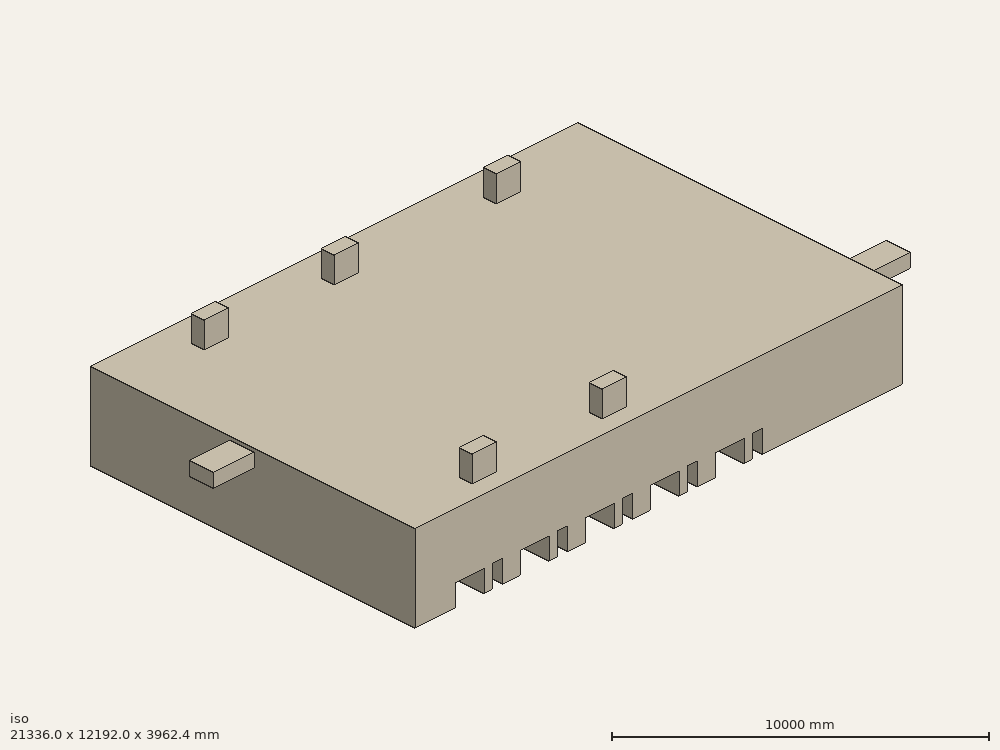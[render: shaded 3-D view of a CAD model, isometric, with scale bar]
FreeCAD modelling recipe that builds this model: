
FCSTD DOCUMENT  (FreeCAD 0.18R14555 (Git shallow))
Label: flow_domain
License: All rights reserved
LicenseURL: http://en.wikipedia.org/wiki/All_rights_reserved
objects: Part::Box×19, Part::MultiFuse×12, Part::Mirroring×1, Part::Cut×1
note: 33 computed .brp shape members not serialized (recipe doc carries the construction recipe); baked Part::Feature solids carry a one-line shape summary decoded from their .brp

FEATURE [Part::Box] Box001  label="Bed 1"
  AttacherType = Attacher::AttachEngine3D
  Height = 762
  Length = 1066.8
  Width = 1981.2
FEATURE [Part::Box] Box002  label="Table 1"
  AttacherType = Attacher::AttachEngine3D
  Height = 798.576
  Length = 396.24
  Placement = pos=(1371.6,0,0) rot=(0,0,1;0rad)
  Width = 396.24
FEATURE [Part::MultiFuse] Fusion  label="Set 1"
  Shapes = -> [Box002,Box001]
FEATURE [Part::Box] Box003  label="Bed 002"
  AttacherType = Attacher::AttachEngine3D
  Height = 762
  Length = 1066.8
  Width = 1981.2
FEATURE [Part::Box] Box004  label="Table 002"
  AttacherType = Attacher::AttachEngine3D
  Height = 798.576
  Length = 396.24
  Placement = pos=(1371.6,0,0) rot=(0,0,1;0rad)
  Width = 396.24
FEATURE [Part::MultiFuse] Fusion001  label="Set 2"
  Placement = pos=(2438.4,0,0) rot=(0,0,1;0rad)
  Shapes = -> [Box004,Box003]
FEATURE [Part::Box] Box005  label="Table 003"
  AttacherType = Attacher::AttachEngine3D
  Height = 798.576
  Length = 396.24
  Placement = pos=(1371.6,0,0) rot=(0,0,1;0rad)
  Width = 396.24
FEATURE [Part::Box] Box006  label="Bed 003"
  AttacherType = Attacher::AttachEngine3D
  Height = 762
  Length = 1066.8
  Width = 1981.2
FEATURE [Part::MultiFuse] Fusion002  label="Set 3"
  Placement = pos=(4876.8,0,0) rot=(0,0,1;0rad)
  Shapes = -> [Box005,Box006]
FEATURE [Part::Box] Box007  label="Bed 004"
  AttacherType = Attacher::AttachEngine3D
  Height = 762
  Length = 1066.8
  Width = 1981.2
FEATURE [Part::Box] Box008  label="Table 004"
  AttacherType = Attacher::AttachEngine3D
  Height = 798.576
  Length = 396.24
  Placement = pos=(1371.6,0,0) rot=(0,0,1;0rad)
  Width = 396.24
FEATURE [Part::MultiFuse] Fusion003  label="Set 4"
  Placement = pos=(7315.2,0,0) rot=(0,0,1;0rad)
  Shapes = -> [Box008,Box007]
FEATURE [Part::Box] Box009  label="Table 005"
  AttacherType = Attacher::AttachEngine3D
  Height = 798.576
  Length = 396.24
  Placement = pos=(1371.6,0,0) rot=(0,0,1;0rad)
  Width = 396.24
FEATURE [Part::Box] Box010  label="Bed 005"
  AttacherType = Attacher::AttachEngine3D
  Height = 762
  Length = 1066.8
  Width = 1981.2
FEATURE [Part::MultiFuse] Fusion004  label="Set 5"
  Placement = pos=(9753.6,0,0) rot=(0,0,1;0rad)
  Shapes = -> [Box009,Box010]
FEATURE [Part::MultiFuse] Fusion005  label="right beds"
  Shapes = -> [Fusion001,Fusion002,Fusion003,Fusion004,Fusion]
FEATURE [Part::Mirroring] Part__Mirroring  label="left beds"
  Base = (0,6096,0)
  Normal = (0,1,0)
  Source = -> Fusion005
FEATURE [Part::Box] Box011  label="Nurse Station"
  AttacherType = Attacher::AttachEngine3D
  Height = 1219.2
  Length = 3048
  Placement = pos=(15240,7620,0) rot=(0,0,1;0rad)
  Width = 4572
FEATURE [Part::Box] Box012  label="main inlet"
  AttacherType = Attacher::AttachEngine3D
  Height = 487.68
  Length = 2438.4
  Placement = pos=(17373.6,1219.2,2438.4) rot=(0,0,1;0rad)
  Width = 914.4
FEATURE [Part::Box] Box013  label="main outlet"
  AttacherType = Attacher::AttachEngine3D
  Height = 487.68
  Length = 2438.4
  Placement = pos=(-1524,6040.43,2438.4) rot=(0,0,1;0rad)
  Width = 914.4
FEATURE [Part::Box] Box014  label="branch"
  AttacherType = Attacher::AttachEngine3D
  Height = 1219.2
  Length = 914.4
  Placement = pos=(14020.8,10668,2743.2) rot=(0,0,1;0rad)
  Width = 487.68
FEATURE [Part::Box] Box016  label="branch002"
  AttacherType = Attacher::AttachEngine3D
  Height = 1219.2
  Length = 914.4
  Placement = pos=(7924.8,609.6,2743.2) rot=(0,0,1;0rad)
  Width = 487.68
FEATURE [Part::Box] Box017  label="branch003"
  AttacherType = Attacher::AttachEngine3D
  Height = 1219.2
  Length = 914.4
  Placement = pos=(7924.8,10668,2743.2) rot=(0,0,1;0rad)
  Width = 487.68
FEATURE [Part::Box] Box018  label="branch004"
  AttacherType = Attacher::AttachEngine3D
  Height = 1219.2
  Length = 914.4
  Placement = pos=(3048,609.6,2743.2) rot=(0,0,1;0rad)
  Width = 487.68
FEATURE [Part::Box] Box019  label="branch005"
  AttacherType = Attacher::AttachEngine3D
  Height = 1219.2
  Length = 914.4
  Placement = pos=(3048,10668,2743.2) rot=(0,0,1;0rad)
  Width = 487.68
FEATURE [Part::MultiFuse] Fusion006  label="all beds"
  Placement = pos=(1524,0,0) rot=(0,0,1;0rad)
  Shapes = -> [Part__Mirroring,Fusion005]
FEATURE [Part::Box] Box  label="Room"
  AttacherType = Attacher::AttachEngine3D
  Height = 3048
  Length = 18288
  Width = 12192
FEATURE [Part::MultiFuse] Fusion007  label="main_ducts"
  Shapes = -> [Box013,Box012]
FEATURE [Part::MultiFuse] Fusion008  label="branch_ducts"
  Placement = pos=(-297.729,0,0) rot=(0,0,1;0rad)
  Shapes = -> [Box014,Box016,Box017,Box018,Box019]
FEATURE [Part::MultiFuse] Fusion009  label="vents"
  Shapes = -> [Fusion008,Fusion007]
FEATURE [Part::MultiFuse] Fusion010  label="surfaces"
  Shapes = -> [Fusion006,Box011]
FEATURE [Part::MultiFuse] Fusion011
  Shapes = -> [Box,Fusion009]
FEATURE [Part::Cut] Cut
  Base = -> Fusion011
  Tool = -> Fusion010
